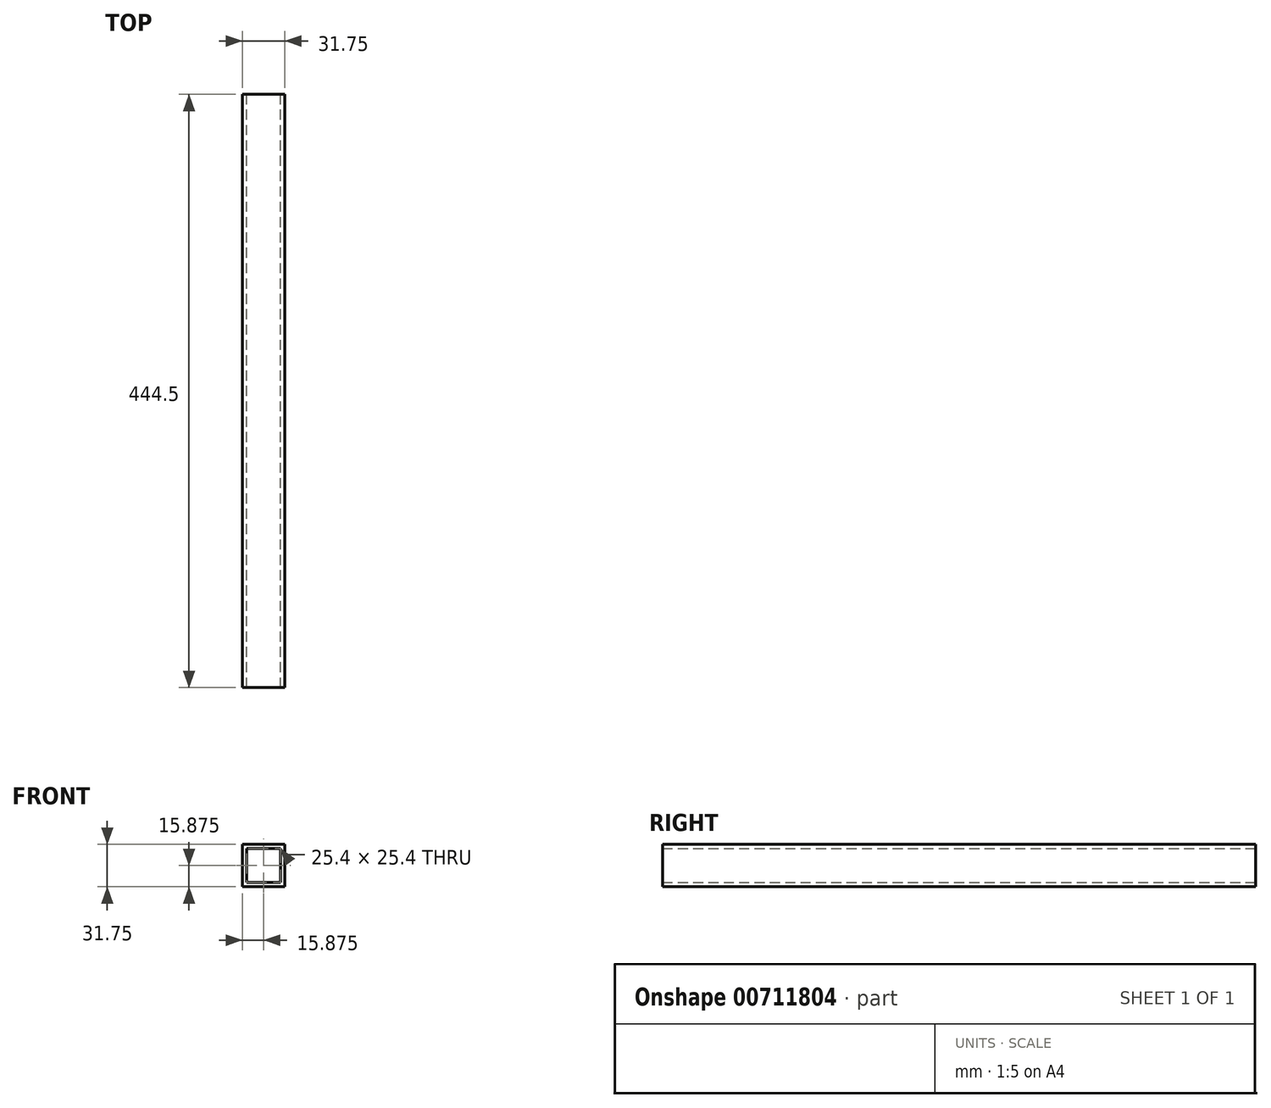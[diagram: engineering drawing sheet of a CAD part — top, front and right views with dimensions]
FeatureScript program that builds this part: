
annotation { "Feature Type Name" : "Feature", "Feature Type Description" : "" }
export const myFeature = defineFeature(function(context is Context, id is Id, definition is map)
    precondition{}
    {
        {
            var Q0;
            Q0=qCreatedBy(makeId("Front.planeOp"),FACE);
            var sketch = newSketch(context, id + "F0", { "sketchPlane" : qUnion([Q0])});
            skLineSegment(sketch, "E0.bottom", {"start": v(0, 0) * mm, "end": v(31.75, 0) * mm});
            skLineSegment(sketch, "E0.top", {"start": v(0, 31.75) * mm, "end": v(31.75, 31.75) * mm});
            skLineSegment(sketch, "E0.left", {"start": v(0, 0) * mm, "end": v(0, 31.75) * mm});
            skLineSegment(sketch, "E0.right", {"start": v(31.75, 0) * mm, "end": v(31.75, 31.75) * mm});
            skLineSegment(sketch, "E1.bottom", {"start": v(3.18, 3.18) * mm, "end": v(28.58, 3.18) * mm});
            skLineSegment(sketch, "E1.top", {"start": v(3.17, 28.58) * mm, "end": v(28.57, 28.58) * mm});
            skLineSegment(sketch, "E1.left", {"start": v(3.17, 3.18) * mm, "end": v(3.17, 28.58) * mm});
            skLineSegment(sketch, "E1.right", {"start": v(28.58, 3.18) * mm, "end": v(28.57, 28.58) * mm});
            skSolve(sketch);
        }
        {
            var Q0;
            Q0 = qSketchRegion(id + "F0", true);
            extrude(context, id + "F1", {"entities" : qUnion([Q0]), "depth" : 444.5 * mm, "offsetDistance" : 25.4 * mm});
        }
    });
